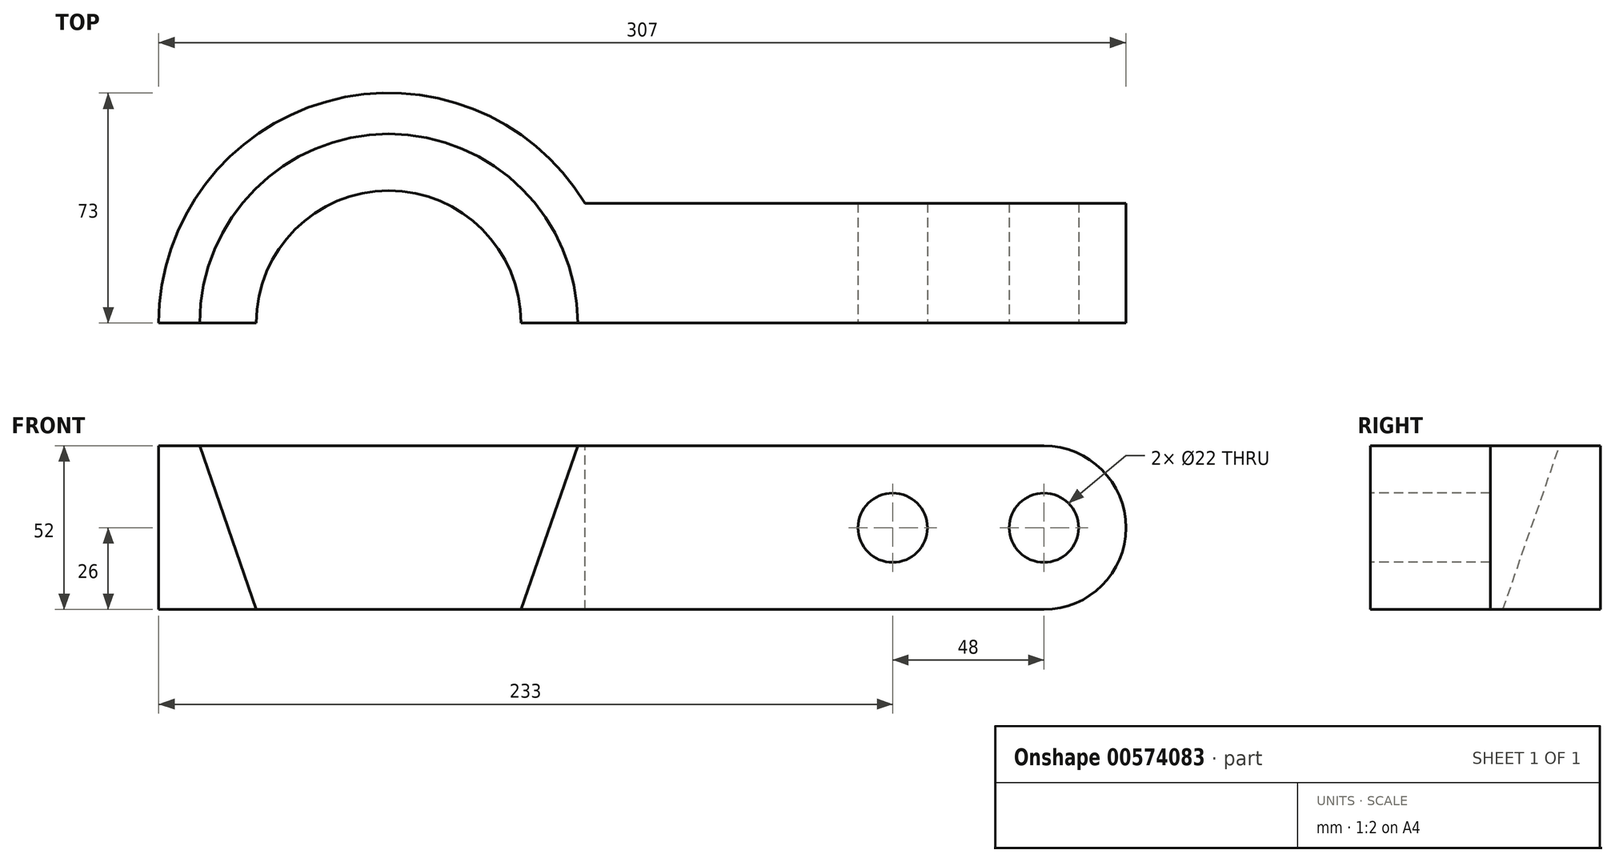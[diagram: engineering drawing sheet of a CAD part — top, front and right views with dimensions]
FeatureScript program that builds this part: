
annotation { "Feature Type Name" : "Feature", "Feature Type Description" : "" }
export const myFeature = defineFeature(function(context is Context, id is Id, definition is map)
    precondition{}
    {
        {
            var Q0;
            Q0=qCreatedBy(makeId("Front.planeOp"),FACE);
            var sketch = newSketch(context, id + "F0", { "sketchPlane" : qUnion([Q0])});
            skLineSegment(sketch, "E0", {"start": v(-42, 0) * mm, "end": v(-60, 52) * mm});
            skLineSegment(sketch, "E1", {"start": v(-60, 52) * mm, "end": v(-73, 52) * mm});
            skLineSegment(sketch, "E2", {"start": v(-73, 52) * mm, "end": v(-73, 0) * mm});
            skLineSegment(sketch, "E3", {"start": v(-73, 0) * mm, "end": v(-42, 0) * mm});
            skLineSegment(sketch, "E4", {"start": v(0, 67.24) * mm, "end": v(0, -14.5) * mm, "construction": true});
            skSolve(sketch);
        }
        {
            var Q0;
            Q0=makeQuery(id+"F0.imprint","IMPRINT",FACE,{"disambiguationData":[TD([[makeQuery(id+"F0.imprint","IMPRINT",EDGE,{"derivedFrom":sQuery(id+"F0.wireOp",EDGE,"E0")}),1.0]])]});
            var Q1;
            Q1=sQuery(id+"F0.wireOp",EDGE,"E4");
            revolve(context, id + "F1", {"entities" : qUnion([Q0]), "axis" : qUnion([Q1]), "revolveType" : RevolveType.ONE_DIRECTION, "angle" : 180 * degree});
        }
        {
            var Q0;
            Q0=qCreatedBy(makeId("Front.planeOp"),FACE);
            var sketch = newSketch(context, id + "F2", { "sketchPlane" : qUnion([Q0])});
            skLineSegment(sketch, "E5.bottom", {"start": v(60, 0) * mm, "end": v(208, 0) * mm});
            skLineSegment(sketch, "E5.top", {"start": v(60, 52) * mm, "end": v(208, 52) * mm});
            skLineSegment(sketch, "E5.left", {"start": v(60, 0) * mm, "end": v(60, 52) * mm});
            skLineSegment(sketch, "E6.0", {"start": v(60, 52) * mm, "end": v(73, 52) * mm});
            skCircle(sketch, "E7", {"center": v(160, 26) * mm, "radius": 11 * mm});
            skCircle(sketch, "E8", {"center": v(208, 26) * mm, "radius": 11 * mm});
            skArc(sketch, "E9", {"start": v(208, 0) * mm, "mid": v(234, 26) * mm, "end": v(208, 52) * mm});
            skSolve(sketch);
        }
        {
            var Q0;
            Q0 = qSketchRegion(id + "F2", true);
            extrude(context, id + "F3", {"entities" : qUnion([Q0]), "operationType" : NewBodyOperationType.ADD, "oppositeDirection" : true, "depth" : 38 * mm, "offsetDistance" : 25 * mm});
        }
    });
